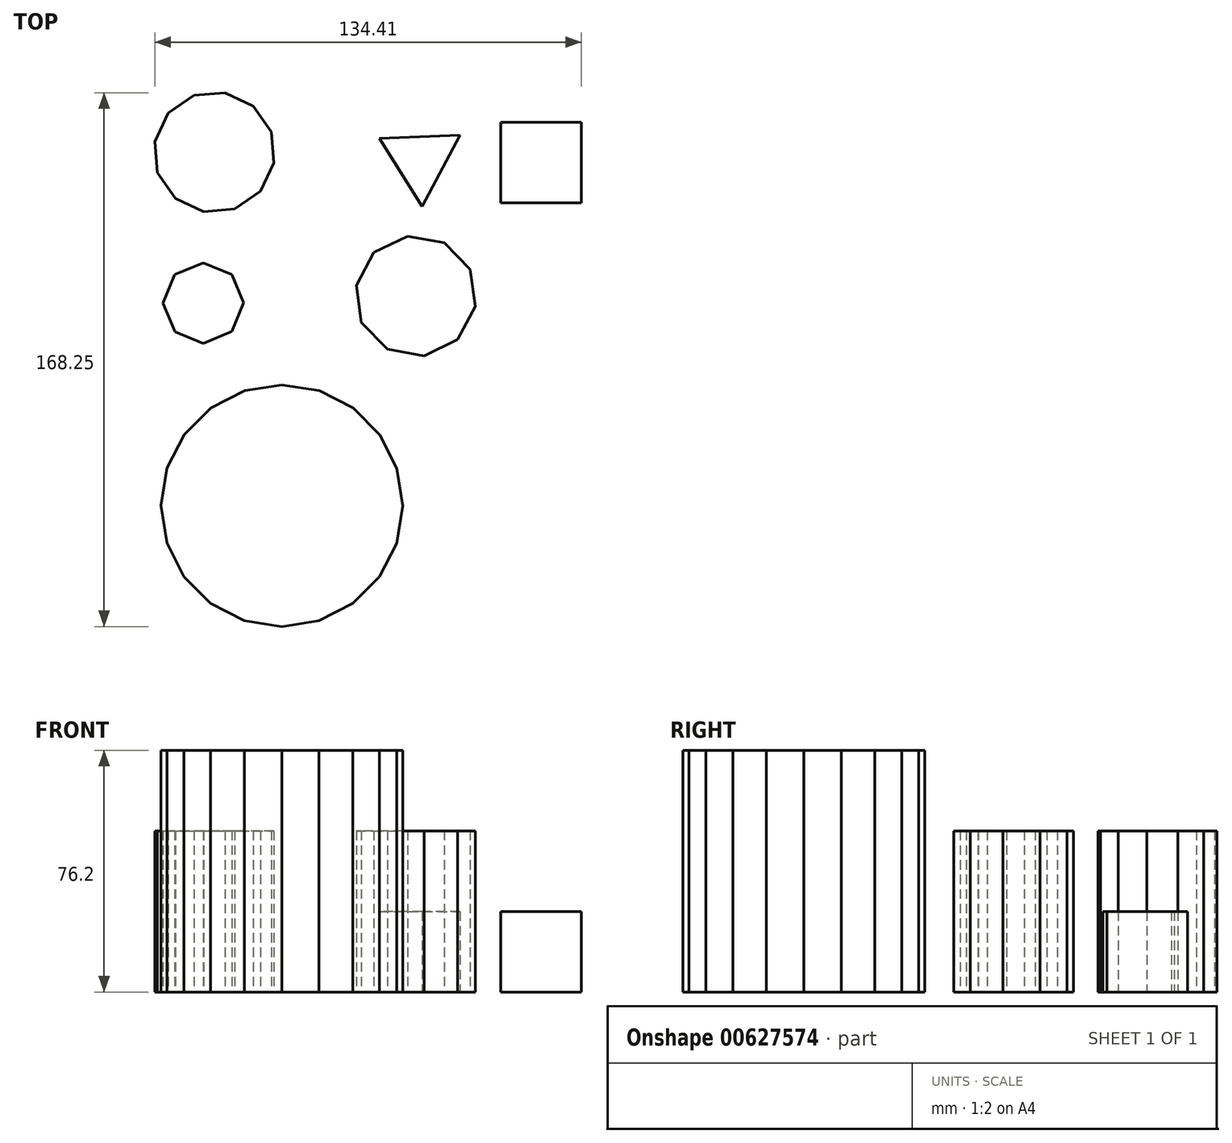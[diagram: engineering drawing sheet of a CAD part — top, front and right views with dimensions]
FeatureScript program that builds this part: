
annotation { "Feature Type Name" : "Feature", "Feature Type Description" : "" }
export const myFeature = defineFeature(function(context is Context, id is Id, definition is map)
    precondition{}
    {
        {
            var Q0;
            Q0=qCreatedBy(makeId("Top.planeOp"),FACE);
            var sketch = newSketch(context, id + "F0", { "sketchPlane" : qUnion([Q0])});
            skCircle(sketch, "E0.cCircle", {"center": v(13.8, 37.2) * mm, "radius": 7.33 * mm, "construction": true});
            skLineSegment(sketch, "E0.0", {"start": v(26.22, 45.01) * mm, "end": v(14.38, 22.54) * mm});
            skLineSegment(sketch, "E0.1", {"start": v(14.38, 22.54) * mm, "end": v(0.84, 44.04) * mm});
            skLineSegment(sketch, "E0.2", {"start": v(0.84, 44.04) * mm, "end": v(26.22, 45.01) * mm});
            skPoint(sketch, "E0.0.midPoint", {"position": v(20.3, 33.78) * mm});
            skSolve(sketch);
        }
        {
            var Q0;
            Q0 = qSketchRegion(id + "F0", true);
            extrude(context, id + "F1", {"entities" : qUnion([Q0]), "depth" : 25.4 * mm, "offsetDistance" : 25.4 * mm});
        }
        {
            var Q0;
            Q0=qCreatedBy(makeId("Top.planeOp"),FACE);
            var sketch = newSketch(context, id + "F2", { "sketchPlane" : qUnion([Q0])});
            skCircle(sketch, "E1.cCircle", {"center": v(-51.13, 39.7) * mm, "radius": 18.4 * mm, "construction": true});
            skLineSegment(sketch, "E1.0", {"start": v(-36.6, 27.39) * mm, "end": v(-44.7, 21.77) * mm});
            skLineSegment(sketch, "E1.1", {"start": v(-44.7, 21.77) * mm, "end": v(-54.52, 20.95) * mm});
            skLineSegment(sketch, "E1.2", {"start": v(-54.52, 20.95) * mm, "end": v(-63.44, 25.16) * mm});
            skLineSegment(sketch, "E1.3", {"start": v(-63.44, 25.16) * mm, "end": v(-69.06, 33.26) * mm});
            skLineSegment(sketch, "E1.4", {"start": v(-69.06, 33.26) * mm, "end": v(-69.87, 43.1) * mm});
            skLineSegment(sketch, "E1.5", {"start": v(-69.87, 43.1) * mm, "end": v(-65.67, 52) * mm});
            skLineSegment(sketch, "E1.6", {"start": v(-65.67, 52) * mm, "end": v(-57.56, 57.63) * mm});
            skLineSegment(sketch, "E1.7", {"start": v(-57.56, 57.63) * mm, "end": v(-47.74, 58.44) * mm});
            skLineSegment(sketch, "E1.8", {"start": v(-47.74, 58.44) * mm, "end": v(-38.82, 54.24) * mm});
            skLineSegment(sketch, "E1.9", {"start": v(-38.82, 54.24) * mm, "end": v(-33.2, 46.13) * mm});
            skLineSegment(sketch, "E1.10", {"start": v(-33.2, 46.13) * mm, "end": v(-32.38, 36.3) * mm});
            skLineSegment(sketch, "E1.11", {"start": v(-32.38, 36.3) * mm, "end": v(-36.6, 27.39) * mm});
            skPoint(sketch, "E1.0.midPoint", {"position": v(-40.64, 24.58) * mm});
            skSolve(sketch);
        }
        {
            var Q0;
            Q0 = qSketchRegion(id + "F2", true);
            extrude(context, id + "F3", {"entities" : qUnion([Q0]), "depth" : 50.8 * mm, "offsetDistance" : 25.4 * mm});
        }
        {
            var Q0;
            Q0=qCreatedBy(makeId("Top.planeOp"),FACE);
            var sketch = newSketch(context, id + "F4", { "sketchPlane" : qUnion([Q0])});
            skLineSegment(sketch, "E2.bottom", {"start": v(39.14, 49.2) * mm, "end": v(64.54, 49.2) * mm});
            skLineSegment(sketch, "E2.top", {"start": v(39.14, 23.8) * mm, "end": v(64.54, 23.8) * mm});
            skLineSegment(sketch, "E2.left", {"start": v(39.14, 49.2) * mm, "end": v(39.14, 23.8) * mm});
            skLineSegment(sketch, "E2.right", {"start": v(64.54, 49.2) * mm, "end": v(64.54, 23.8) * mm});
            skSolve(sketch);
        }
        {
            var Q0;
            Q0 = qSketchRegion(id + "F4", true);
            extrude(context, id + "F5", {"entities" : qUnion([Q0]), "depth" : 25.4 * mm, "offsetDistance" : 25.4 * mm});
        }
        {
            var Q0;
            Q0=qCreatedBy(makeId("Top.planeOp"),FACE);
            var sketch = newSketch(context, id + "F6", { "sketchPlane" : qUnion([Q0])});
            skCircle(sketch, "E3.cCircle", {"center": v(-54.6, -7.86) * mm, "radius": 11.73 * mm, "construction": true});
            skLineSegment(sketch, "E3.0", {"start": v(-41.9, -7.82) * mm, "end": v(-45.6, -16.81) * mm});
            skLineSegment(sketch, "E3.1", {"start": v(-45.6, -16.81) * mm, "end": v(-54.56, -20.56) * mm});
            skLineSegment(sketch, "E3.2", {"start": v(-54.56, -20.56) * mm, "end": v(-63.55, -16.87) * mm});
            skLineSegment(sketch, "E3.3", {"start": v(-63.55, -16.87) * mm, "end": v(-67.3, -7.9) * mm});
            skLineSegment(sketch, "E3.4", {"start": v(-67.3, -7.9) * mm, "end": v(-63.6, 1.1) * mm});
            skLineSegment(sketch, "E3.5", {"start": v(-63.6, 1.1) * mm, "end": v(-54.64, 4.84) * mm});
            skLineSegment(sketch, "E3.6", {"start": v(-54.64, 4.84) * mm, "end": v(-45.65, 1.15) * mm});
            skLineSegment(sketch, "E3.7", {"start": v(-45.65, 1.15) * mm, "end": v(-41.9, -7.82) * mm});
            skPoint(sketch, "E3.0.midPoint", {"position": v(-43.75, -12.32) * mm});
            skSolve(sketch);
        }
        {
            var Q0;
            Q0 = qSketchRegion(id + "F6", true);
            extrude(context, id + "F7", {"entities" : qUnion([Q0]), "depth" : 50.8 * mm, "offsetDistance" : 25.4 * mm});
        }
        {
            var Q0;
            Q0=qCreatedBy(makeId("Top.planeOp"),FACE);
            var sketch = newSketch(context, id + "F8", { "sketchPlane" : qUnion([Q0])});
            skCircle(sketch, "E4.cCircle", {"center": v(12.35, -5.61) * mm, "radius": 18.12 * mm, "construction": true});
            skLineSegment(sketch, "E4.0", {"start": v(31.1, -8.94) * mm, "end": v(25.56, -19.33) * mm});
            skLineSegment(sketch, "E4.1", {"start": v(25.56, -19.33) * mm, "end": v(14.98, -24.48) * mm});
            skLineSegment(sketch, "E4.2", {"start": v(14.98, -24.48) * mm, "end": v(3.38, -22.42) * mm});
            skLineSegment(sketch, "E4.3", {"start": v(3.38, -22.42) * mm, "end": v(-4.78, -13.94) * mm});
            skLineSegment(sketch, "E4.4", {"start": v(-4.78, -13.94) * mm, "end": v(-6.4, -2.28) * mm});
            skLineSegment(sketch, "E4.5", {"start": v(-6.4, -2.28) * mm, "end": v(-0.87, 8.1) * mm});
            skLineSegment(sketch, "E4.6", {"start": v(-0.87, 8.1) * mm, "end": v(9.72, 13.25) * mm});
            skLineSegment(sketch, "E4.7", {"start": v(9.72, 13.25) * mm, "end": v(21.31, 11.2) * mm});
            skLineSegment(sketch, "E4.8", {"start": v(21.31, 11.2) * mm, "end": v(29.48, 2.72) * mm});
            skLineSegment(sketch, "E4.9", {"start": v(29.48, 2.72) * mm, "end": v(31.1, -8.94) * mm});
            skPoint(sketch, "E4.0.midPoint", {"position": v(28.33, -14.14) * mm});
            skSolve(sketch);
        }
        {
            var Q0;
            Q0 = qSketchRegion(id + "F8", true);
            extrude(context, id + "F9", {"entities" : qUnion([Q0]), "depth" : 50.8 * mm, "offsetDistance" : 25.4 * mm});
        }
        {
            var Q0;
            Q0=qCreatedBy(makeId("Top.planeOp"),FACE);
            var sketch = newSketch(context, id + "F10", { "sketchPlane" : qUnion([Q0])});
            skCircle(sketch, "E5.cCircle", {"center": v(-29.85, -71.71) * mm, "radius": 37.63 * mm, "construction": true});
            skLineSegment(sketch, "E5.0", {"start": v(6.4, -59.98) * mm, "end": v(8.25, -71.76) * mm});
            skLineSegment(sketch, "E5.1", {"start": v(8.25, -71.76) * mm, "end": v(6.37, -83.53) * mm});
            skLineSegment(sketch, "E5.2", {"start": v(6.37, -83.53) * mm, "end": v(0.95, -94.14) * mm});
            skLineSegment(sketch, "E5.3", {"start": v(0.95, -94.14) * mm, "end": v(-7.5, -102.56) * mm});
            skLineSegment(sketch, "E5.4", {"start": v(-7.5, -102.56) * mm, "end": v(-18.12, -107.96) * mm});
            skLineSegment(sketch, "E5.5", {"start": v(-18.12, -107.96) * mm, "end": v(-29.9, -109.81) * mm});
            skLineSegment(sketch, "E5.6", {"start": v(-29.9, -109.81) * mm, "end": v(-41.67, -107.93) * mm});
            skLineSegment(sketch, "E5.7", {"start": v(-41.67, -107.93) * mm, "end": v(-52.28, -102.5) * mm});
            skLineSegment(sketch, "E5.8", {"start": v(-52.28, -102.5) * mm, "end": v(-60.7, -94.07) * mm});
            skLineSegment(sketch, "E5.9", {"start": v(-60.7, -94.07) * mm, "end": v(-66.1, -83.44) * mm});
            skLineSegment(sketch, "E5.10", {"start": v(-66.1, -83.44) * mm, "end": v(-67.95, -71.67) * mm});
            skLineSegment(sketch, "E5.11", {"start": v(-67.95, -71.67) * mm, "end": v(-66.07, -59.9) * mm});
            skLineSegment(sketch, "E5.12", {"start": v(-66.07, -59.9) * mm, "end": v(-60.65, -49.28) * mm});
            skLineSegment(sketch, "E5.13", {"start": v(-60.65, -49.28) * mm, "end": v(-52.2, -40.86) * mm});
            skLineSegment(sketch, "E5.14", {"start": v(-52.2, -40.86) * mm, "end": v(-41.58, -35.46) * mm});
            skLineSegment(sketch, "E5.15", {"start": v(-41.58, -35.46) * mm, "end": v(-29.8, -33.61) * mm});
            skLineSegment(sketch, "E5.16", {"start": v(-29.8, -33.61) * mm, "end": v(-18.03, -35.5) * mm});
            skLineSegment(sketch, "E5.17", {"start": v(-18.03, -35.5) * mm, "end": v(-7.42, -40.92) * mm});
            skLineSegment(sketch, "E5.18", {"start": v(-7.42, -40.92) * mm, "end": v(1, -49.35) * mm});
            skLineSegment(sketch, "E5.19", {"start": v(1, -49.35) * mm, "end": v(6.4, -59.98) * mm});
            skPoint(sketch, "E5.0.midPoint", {"position": v(7.32, -65.87) * mm});
            skSolve(sketch);
        }
        {
            var Q0;
            Q0 = qSketchRegion(id + "F10", true);
            extrude(context, id + "F11", {"entities" : qUnion([Q0]), "depth" : 76.2 * mm, "offsetDistance" : 25.4 * mm});
        }
    });
